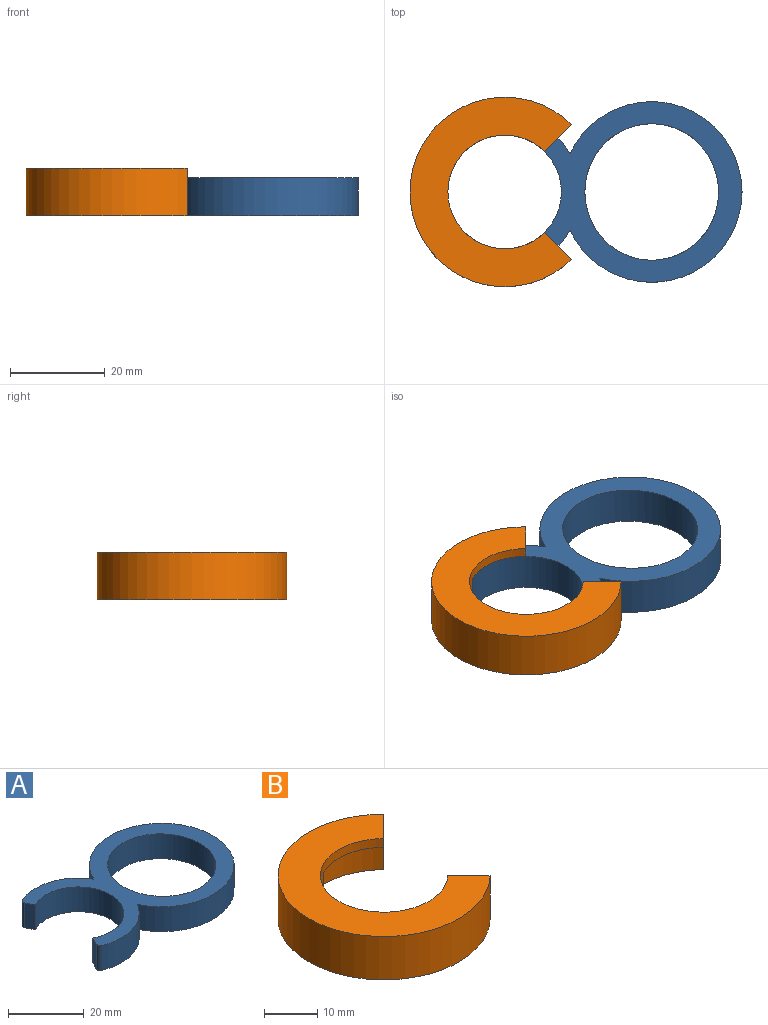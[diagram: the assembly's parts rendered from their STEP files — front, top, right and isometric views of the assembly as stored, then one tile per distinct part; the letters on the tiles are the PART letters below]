
ASSEMBLY  parts=2 mates=1
PART A: 11 faces, bbox 56.9x38.1x8 mm
  f0: cylinder r=16mm len=19.98mm, axis (0,0,-1), area 183.7mm2, adj f5,f6,f7,f9
  f1: cylinder r=16mm len=19.96mm, axis (0,0,-1), area 183.6mm2, adj f5,f6,f7,f10
  f2: cylinder r=12mm len=24mm, axis (0,0,-1), area 390mm2, adj f3,f4,f5,f6
  f3: plane 8x2.64mm, normal (-0.89,0.45,0), area 23.7mm2, adj f2,f5,f6,f9
  f4: plane 8x2.62mm, normal (-0.89,-0.45,0), area 23.4mm2, adj f2,f5,f6,f10
  f5: plane 56.88x38.11mm, normal (0,0,1), area 686.9mm2, adj f0,f1,f2,f3,f4,f7,f8,f9
  f6: plane 56.88x38.11mm, normal (0,0,-1), area 686.9mm2, adj f0,f1,f2,f3,f4,f7,f8,f9
  f7: cylinder r=19.06mm len=38.11mm, axis (0,0,-1), area 823.2mm2, adj f0,f1,f5,f6
  f8: extruded ~28.8x28.2mm, area 716.3mm2, adj f5,f6
  f9: cylinder r=1mm len=8mm, axis (0,0,-1), area 13.1mm2, adj f0,f3,f5,f6
  f10: cylinder r=1mm len=8mm, axis (0,0,-1), area 13.1mm2, adj f1,f4,f5,f6
PART B: 12 faces, bbox 34x40x10 mm
  f0: cylinder r=12mm len=24mm, axis (0,0,-1), area 323.8mm2, adj f1,f2,f5,f6,f7,f8,f10,f11
  f1: plane 40x34.03mm, normal (0,0,1), area 601.1mm2, adj f0,f4,f10,f11
  f2: plane 18.49x7.45mm, normal (0,0,-1), area 69.9mm2, adj f0,f3,f8,f11
  f3: cylinder r=16mm len=18.49mm, axis (0,0,-1), area 159.8mm2, adj f2,f5,f8,f11
  f4: cylinder r=20mm len=40mm, axis (0,0,-1), area 939.2mm2, adj f1,f5,f10,f11
  f5: plane 40x34.03mm, normal (0,0,-1), area 461.3mm2, adj f0,f3,f4,f7,f8,f9,f10,f11
  f6: plane 18.49x7.45mm, normal (0,0,-1), area 69.9mm2, adj f0,f7,f9,f10
  f7: plane 8x3.56mm, normal (0.89,0.45,0), area 32mm2, adj f0,f5,f6,f9
  f8: plane 8x3.56mm, normal (0.89,-0.45,0), area 32mm2, adj f0,f2,f3,f5
  f9: cylinder r=16mm len=18.49mm, axis (0,0,-1), area 159.8mm2, adj f5,f6,f7,f10
  f10: plane 10x5.7mm, normal (0.71,-0.7,0), area 48mm2, adj f0,f1,f4,f5,f6,f9
  f11: plane 10x5.7mm, normal (0.71,0.7,0), area 48mm2, adj f0,f1,f2,f3,f4,f5
PLACE A t=(-3.63,7.89,-4.49)mm
PLACE B t=(63.38,7.89,-4.51)mm
MATE cylindrical B.f0 <-> A.f0  axis (0,0,-1) through (-3.63,7.89,0.49)mm
